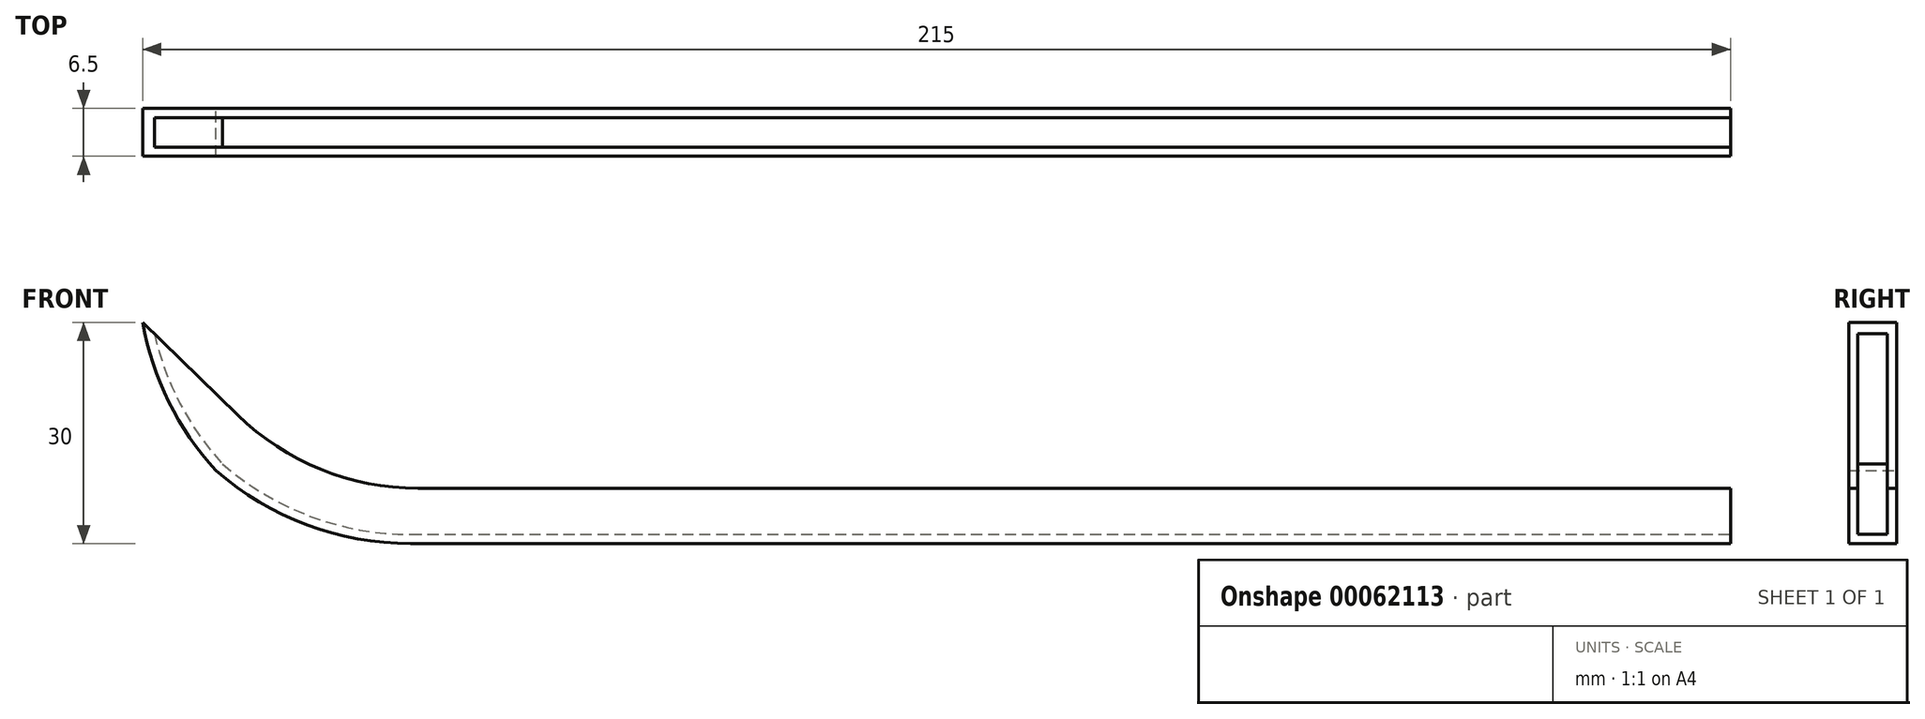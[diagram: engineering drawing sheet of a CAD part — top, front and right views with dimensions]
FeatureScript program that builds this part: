
annotation { "Feature Type Name" : "Feature", "Feature Type Description" : "" }
export const myFeature = defineFeature(function(context is Context, id is Id, definition is map)
    precondition{}
    {
        {
            assignVariable(context, id + "F0", {"name" : "WallThickness", "anyValue" : 1.25});
        }
        {
            assignVariable(context, id + "F1", {"name" : "Width", "anyValue" : 6.5});
        }
        {
            var Q0;
            Q0=qCreatedBy(makeId("Front.planeOp"),FACE);
            var sketch = newSketch(context, id + "F2", { "sketchPlane" : qUnion([Q0])});
            skLineSegment(sketch, "E0", {"start": v(20, 0) * mm, "end": v(215, 0) * mm});
            skLineSegment(sketch, "E1", {"start": v(215, 0) * mm, "end": v(215, 7.5) * mm});
            skLineSegment(sketch, "E2", {"start": v(215, 7.5) * mm, "end": v(23.05, 7.5) * mm});
            skLineSegment(sketch, "E3", {"start": v(23.05, 7.5) * mm, "end": v(0, 30) * mm});
            skLineSegment(sketch, "E4", {"start": v(0, 30) * mm, "end": v(0, 19.52) * mm});
            skLineSegment(sketch, "E5", {"start": v(0, 19.52) * mm, "end": v(20, 0) * mm});
            skPoint(sketch, "E6.orphan", {"position": v(0, 0) * mm});
            skSolve(sketch);
        }
        {
            var Q0;
            Q0=makeQuery(id+"F2.imprint","IMPRINT",FACE,{"disambiguationData":[TD([[makeQuery(id+"F2.imprint","IMPRINT",EDGE,{"derivedFrom":sQuery(id+"F2.wireOp",EDGE,"E0")}),1.0]])]});
            extrude(context, id + "F3", {"entities" : qUnion([Q0]), "depth" : (getVariable(context, 'Width')) * mm});
        }
        {
            var Q0;
            Q0=makeQuery(id+"F3.opExtrude","SWEPT_EDGE",EDGE,{"disambiguationData":[OSD([sQuery(id+"F2.wireOp",EDGE,"E0"),sQuery(id+"F2.wireOp",EDGE,"E5")])]});
            var Q1;
            Q1=makeQuery(id+"F3.opExtrude","SWEPT_EDGE",EDGE,{"disambiguationData":[OSD([sQuery(id+"F2.wireOp",EDGE,"E4"),sQuery(id+"F2.wireOp",EDGE,"E5")])]});
            fillet(context, id + "F4", {"entities" : qUnion([Q0, Q1]), "radius" : 40 * mm, "tangentPropagation" : true, "allowEdgeOverflow" : false});
        }
        {
            var Q0;
            Q0=makeQuery(id+"F3.opExtrude","SWEPT_EDGE",EDGE,{"disambiguationData":[OSD([sQuery(id+"F2.wireOp",EDGE,"E2"),sQuery(id+"F2.wireOp",EDGE,"E3")])]});
            fillet(context, id + "F5", {"entities" : qUnion([Q0]), "radius" : 35 * mm, "tangentPropagation" : true, "allowEdgeOverflow" : false});
        }
        {
            var Q0;
            Q0=makeQuery(id+"F3.opExtrude","SWEPT_FACE",FACE,{"disambiguationData":[OSD([sQuery(id+"F2.wireOp",EDGE,"E3")])]});
            var Q1;
            Q1=makeQuery(id+"F5.opFillet","BLEND_FACE",FACE,{"disambiguationData":[OSD([sQuery(id+"F2.wireOp",EDGE,"E2"),sQuery(id+"F2.wireOp",EDGE,"E3")])]});
            var Q2;
            Q2=makeQuery(id+"F3.opExtrude","SWEPT_FACE",FACE,{"disambiguationData":[OSD([sQuery(id+"F2.wireOp",EDGE,"E2")])]});
            var Q3;
            Q3=makeQuery(id+"F3.opExtrude","SWEPT_FACE",FACE,{"disambiguationData":[OSD([sQuery(id+"F2.wireOp",EDGE,"E1")])]});
            shell(context, id + "F6", {"entities" : qUnion([Q0, Q1, Q2, Q3]), "thickness" : (getVariable(context, 'WallThickness')) * mm});
        }
    });
